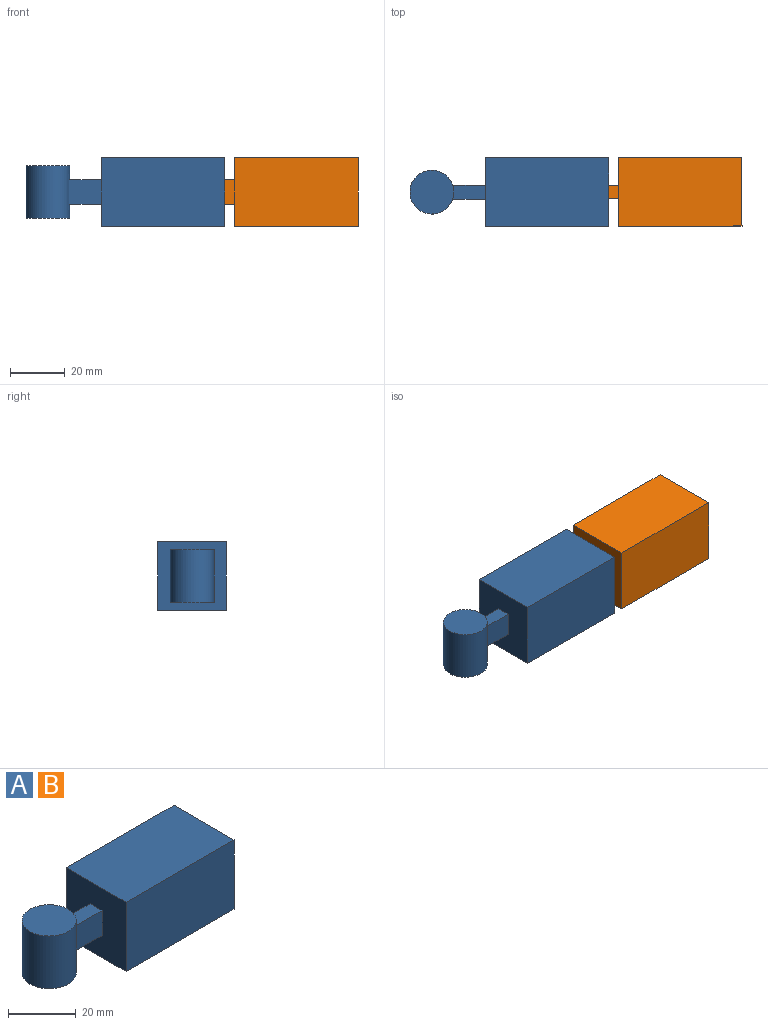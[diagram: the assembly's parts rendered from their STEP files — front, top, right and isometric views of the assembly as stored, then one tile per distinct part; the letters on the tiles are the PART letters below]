
ASSEMBLY  parts=2 mates=1
PART A: 20 faces, bbox 72.6x25x25 mm
  f0: plane 25x25mm, normal (-1,0,0), area 580mm2, adj f1,f3,f4,f5,f6,f7,f8,f9
  f1: plane 45x25mm, normal (0,-1,0), area 1125mm2, adj f0,f2,f4,f5
  f2: plane 25x25mm, normal (1,0,0), area 470mm2, adj f1,f3,f4,f5,f13,f14,f15,f16
  f3: plane 45x25mm, normal (0,1,0), area 1125mm2, adj f0,f2,f4,f5
  f4: plane 45x25mm, normal (0,0,1), area 1125mm2, adj f0,f1,f2,f3
  f5: plane 45x25mm, normal (0,0,-1), area 1125mm2, adj f0,f1,f2,f3
  f6: plane 12x9mm, normal (0,1,0), area 108mm2, adj f0,f8,f9,f10
  f7: plane 12x9mm, normal (0,-1,0), area 108mm2, adj f0,f8,f9,f10
  f8: plane 12x5mm, normal (0,0,1), area 58.7mm2, adj f0,f6,f7,f10
  f9: plane 12x5mm, normal (0,0,-1), area 58.7mm2, adj f0,f6,f7,f10
  f10: cylinder r=8mm len=19mm, axis (0,0,-1), area 909.3mm2, adj f6,f7,f8,f9,f11,f12
  f11: plane 16x16mm, normal (0,0,1), area 201.1mm2, adj f10
  f12: plane 16x16mm, normal (0,0,-1), area 201.1mm2, adj f10
  f13: plane 10x8mm, normal (0.51,-0.86,0), area 93mm2, adj f2,f15,f16,f17
  f14: plane 10x8mm, normal (0.51,0.86,0), area 93mm2, adj f2,f15,f16,f17
  f15: plane 15.5x8mm, normal (0,0,-1), area 83.8mm2, adj f2,f13,f14,f17
  f16: plane 15.5x8mm, normal (0,0,1), area 83.8mm2, adj f2,f13,f14,f17
  f17: cylinder r=8.5mm len=20mm, axis (0,0,-1), area 1006.8mm2, adj f13,f14,f15,f16,f18,f19
  f18: plane 17x17mm, normal (0,0,-1), area 227mm2, adj f17
  f19: plane 17x17mm, normal (0,0,1), area 227mm2, adj f17
PART B: same geometry as A
PLACE A t=(24.89,-8.64,-8.61)mm fixed
PLACE B rot(axis=(0,0,1),0.1deg) t=(73.53,-8.55,-8.61)mm
MATE revolute A.f17 <-> B.f10  axis (0,0,1) through (31.43,-8.64,-18.61)mm
